FCSTD DOCUMENT  (FreeCAD 0.20R29177 +426 (Git))
Label: connector
License: All rights reserved
LicenseURL: http://en.wikipedia.org/wiki/All_rights_reserved
objects: Sketcher::SketchObject×4, PartDesign::AdditiveLoft×1, PartDesign::Body×1
note: 7 computed .brp shape members not serialized (recipe doc carries the construction recipe); baked Part::Feature solids carry a one-line shape summary decoded from their .brp

FEATURE [Sketcher::SketchObject] Sketch  label="outer_c"
  AttachmentOffset = pos=(0,0,8) rot=(0,0,1;0rad)
  FullyConstrained = true
  MapMode = 5
  Placement = pos=(0,0,8) rot=(0,0,1;0rad)
  Support = -> [XY_Plane]
  sketch-geometry (1):
    g0: Circle CenterX=0 CenterY=0 CenterZ=0 NormalX=0 NormalY=0 NormalZ=1 AngleXU=0 Radius=10.5
  constraints (2):
    c: Coincident(g0,g-1)
    c: Radius(g0) = 10.5
FEATURE [Sketcher::SketchObject] Sketch001  label="outer_r"
  FullyConstrained = true
  MapMode = 5
  Support = -> [XY_Plane]
  sketch-geometry (4):
    g0: LineSegment StartX=-16 StartY=12 StartZ=0 EndX=16 EndY=12 EndZ=0
    g1: LineSegment StartX=16 StartY=12 StartZ=0 EndX=16 EndY=-12 EndZ=0
    g2: LineSegment StartX=16 StartY=-12 StartZ=0 EndX=-16 EndY=-12 EndZ=0
    g3: LineSegment StartX=-16 StartY=-12 StartZ=0 EndX=-16 EndY=12 EndZ=0
  constraints (11):
    c: Coincident(g0,g1)
    c: Coincident(g1,g2)
    c: Coincident(g2,g3)
    c: Coincident(g3,g0)
    c: Horizontal(g0)
    c: Horizontal(g2)
    c: Vertical(g1)
    c: Vertical(g3)
    c: DistanceX(g0,g0) = 32
    c: DistanceY(g3,g3) = 24
    c: Symmetric(g0,g1,g-1)
FEATURE [PartDesign::AdditiveLoft] AdditiveLoft
  Closed = false
  Profile = -> Sketch
  Ruled = false
  Sections = -> [Sketch001]
FEATURE [Sketcher::SketchObject] Sketch002  label="inner_c"
  AttachmentOffset = pos=(0,0,8) rot=(0,0,1;0rad)
  FullyConstrained = true
  MapMode = 5
  Placement = pos=(0,0,8) rot=(0,0,1;0rad)
  Support = -> [XY_Plane]
  sketch-geometry (1):
    g0: Circle CenterX=0 CenterY=0 CenterZ=0 NormalX=0 NormalY=0 NormalZ=1 AngleXU=0 Radius=8.5
  constraints (2):
    c: Coincident(g0,g-1)
    c: Radius(g0) = 8.5
FEATURE [Sketcher::SketchObject] Sketch003  label="inner_r"
  FullyConstrained = true
  MapMode = 5
  Support = -> [XY_Plane]
  sketch-geometry (4):
    g0: LineSegment StartX=-11.5 StartY=2.5 StartZ=0 EndX=11.5 EndY=2.5 EndZ=0
    g1: LineSegment StartX=11.5 StartY=2.5 StartZ=0 EndX=11.5 EndY=-2.5 EndZ=0
    g2: LineSegment StartX=11.5 StartY=-2.5 StartZ=0 EndX=-11.5 EndY=-2.5 EndZ=0
    g3: LineSegment StartX=-11.5 StartY=-2.5 StartZ=0 EndX=-11.5 EndY=2.5 EndZ=0
  constraints (11):
    c: Coincident(g0,g1)
    c: Coincident(g1,g2)
    c: Coincident(g2,g3)
    c: Coincident(g3,g0)
    c: Horizontal(g0)
    c: Horizontal(g2)
    c: Vertical(g1)
    c: Vertical(g3)
    c: DistanceX(g0,g0) = 23
    c: DistanceY(g3,g3) = 5
    c: Symmetric(g0,g1,g-1)
FEATURE [PartDesign::Body] Body
  Group = -> [Sketch,Sketch001,AdditiveLoft,Sketch002,Sketch003]
  Origin = -> Origin
